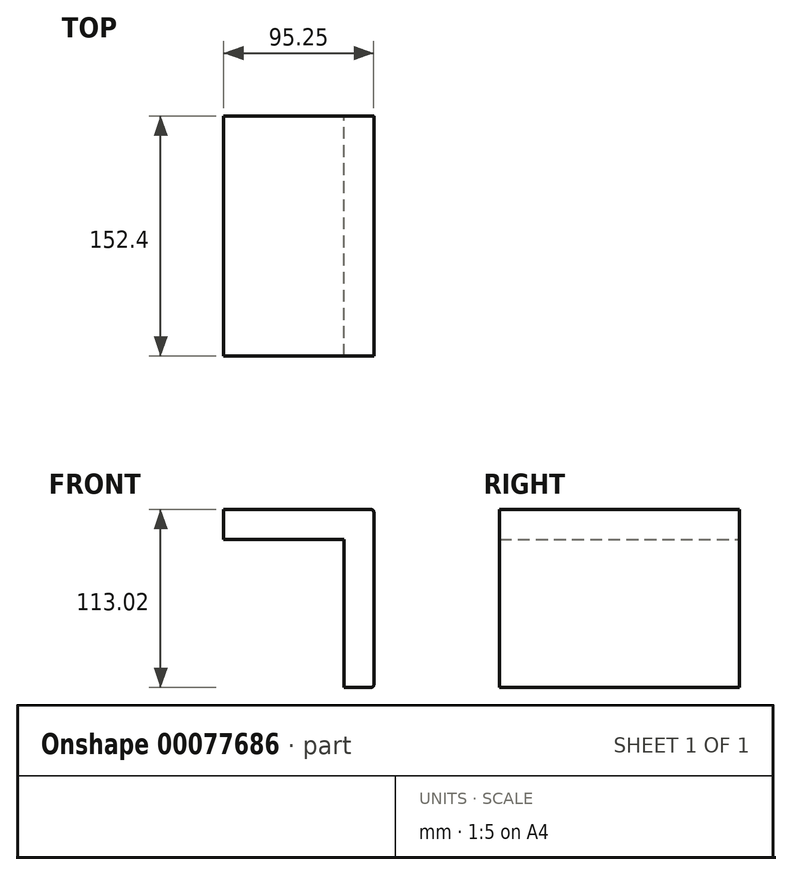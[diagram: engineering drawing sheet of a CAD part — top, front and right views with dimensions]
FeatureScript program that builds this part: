
annotation { "Feature Type Name" : "Feature", "Feature Type Description" : "" }
export const myFeature = defineFeature(function(context is Context, id is Id, definition is map)
    precondition{}
    {
        {
            var Q0;
            Q0=qCreatedBy(makeId("Front.planeOp"),FACE);
            var sketch = newSketch(context, id + "F0", { "sketchPlane" : qUnion([Q0])});
            skLineSegment(sketch, "E0", {"start": v(28.58, 60.33) * mm, "end": v(28.58, -52.7) * mm});
            skLineSegment(sketch, "E1", {"start": v(46.04, 60.33) * mm, "end": v(28.58, 60.33) * mm});
            skLineSegment(sketch, "E2", {"start": v(47.63, -51.12) * mm, "end": v(47.63, 58.74) * mm});
            skLineSegment(sketch, "E3", {"start": v(28.58, -52.7) * mm, "end": v(46.04, -52.7) * mm});
            skLineSegment(sketch, "E4", {"start": v(28.58, 60.33) * mm, "end": v(-47.63, 60.33) * mm});
            skLineSegment(sketch, "E5", {"start": v(-47.63, 60.33) * mm, "end": v(-47.63, 41.28) * mm});
            skLineSegment(sketch, "E6", {"start": v(-47.63, 41.28) * mm, "end": v(28.58, 41.28) * mm});
            skArc(sketch, "E7", {"start": v(46.04, -52.7) * mm, "mid": v(47.16, -52.24) * mm, "end": v(47.62, -51.12) * mm});
            skArc(sketch, "E8", {"start": v(47.62, 58.74) * mm, "mid": v(47.16, 59.86) * mm, "end": v(46.04, 60.33) * mm});
            skSolve(sketch);
        }
        {
            var Q0;
            {var subQ1=sQuery(id+"F0.wireOp",EDGE,"E1");Q0=makeQuery(id+"F0.imprint","IMPRINT",FACE,{"disambiguationData":[TD([[makeQuery(id+"F0.imprint","IMPRINT",EDGE,{"derivedFrom":subQ1}),1.0]])]});}
            var Q1;
            {var subQ0=sQuery(id+"F0.wireOp",EDGE,"E4");Q1=makeQuery(id+"F0.imprint","IMPRINT",FACE,{"disambiguationData":[TD([[makeQuery(id+"F0.imprint","IMPRINT",EDGE,{"derivedFrom":subQ0}),1.0]])]});}
            extrude(context, id + "F1", {"entities" : qUnion([Q0, Q1]), "depth" : 152.4 * mm});
        }
    });
